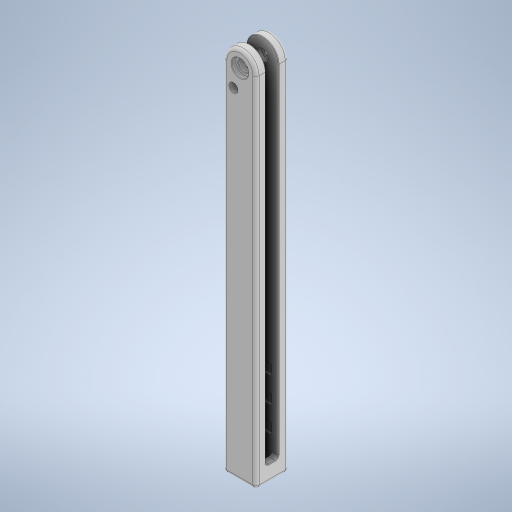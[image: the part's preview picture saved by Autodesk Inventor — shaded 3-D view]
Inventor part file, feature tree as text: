
AUTODESK INVENTOR PART (.ipt)
format: ipt  version: 2023.5 (Build 275446000, 446)  size: 384,000 bytes
history: native  units: mm
features: extrude x6, sketch x5, fillet x2, plane x1, mirror x1, chamfer x1
ambient origin geometry x8: Origin, YZ Plane, XZ Plane, XY Plane, X Axis, Y Axis, Z Axis, Center Point
bodies: Solid1 (feature_tree)
feature tree (16):
  extrude  "Extrusion1"  Depth=12.7mm
  sketch  "Sketch2"  dims[d2=4.572mm d3=12.7mm d4=0.0mm]
  extrude  "Extrusion2"  Depth=12.7mm TaperAngle=0.0deg
  extrude  "Extrusion3"  Depth=5.08mm
  extrude  "Extrusion4"  Depth=120.048mm
  fillet  "Fillet1"  Radius=5.08mm
  extrude  "Extrusion6"  Depth=8.89mm TaperAngle=0.0deg
  plane  "Work Plane1"
  mirror  "Mirror1"
  extrude  "Extrusion7"  TaperAngle=0.0deg  [1 undecoded]
  fillet  "Fillet2"  Radius=3.175mm
  chamfer  "Chamfer1"  Distance=7.954mm
  sketch  "Sketch1"  dims[d0=12.7mm d1=140.97mm]
  sketch  "Sketch3"  dims[d5=6.35mm d6=5.08mm]
  sketch  "Sketch5"  dims[d7=3.81mm d8=120.048mm d9=5.08mm]
  sketch  "Sketch6"  dims[d10=24.0mm d11=8.89mm d12=0.0mm d13=0.0mm d14=0.0mm d15=3.175mm d16=7.954mm d17=2.54mm d18=0.0mm d19=0.0mm d20=1.2mm d25=6.604mm d26=1.651mm d27=0.0mm d29=10.0mm d31=40.0mm d32=7.0mm d33=4.0mm d34=10.0mm d35=10.0mm d36=2.0mm d37=1.5mm d38=10.0mm d39=0.0mm d40=0.2mm d41=0.2mm d42=2.0mm d43=45.0deg]
note: 1 required parameter value undecoded (feature->parameter linkage not recoverable at this tier; creation-order binding heuristic only, values carry confidence <= 0.55)
